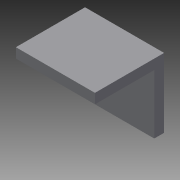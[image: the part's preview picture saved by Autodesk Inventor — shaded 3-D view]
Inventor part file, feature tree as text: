
AUTODESK INVENTOR PART (.ipt)
format: ipt  version: 2013 (Build 170138000, 138)  size: 71,680 bytes
history: native  units: in
note: dims shown in document units (in); Inventor stores cm internally (conversion verified against a paired STEP export)
features: extrude x1, sketch x1
ambient origin geometry x8: Origin, YZ Plane, XZ Plane, XY Plane, X Axis, Y Axis, Z Axis, Center Point
bodies: Solid1 (feature_tree)
feature tree (2):
  extrude  "Extrusion1"  Depth=0.75in
  sketch  "Sketch1"  dims[d0=0.75in d1=0.75in d2=0.125in d3=0.875in d4=1.0in d5=0.0in]
